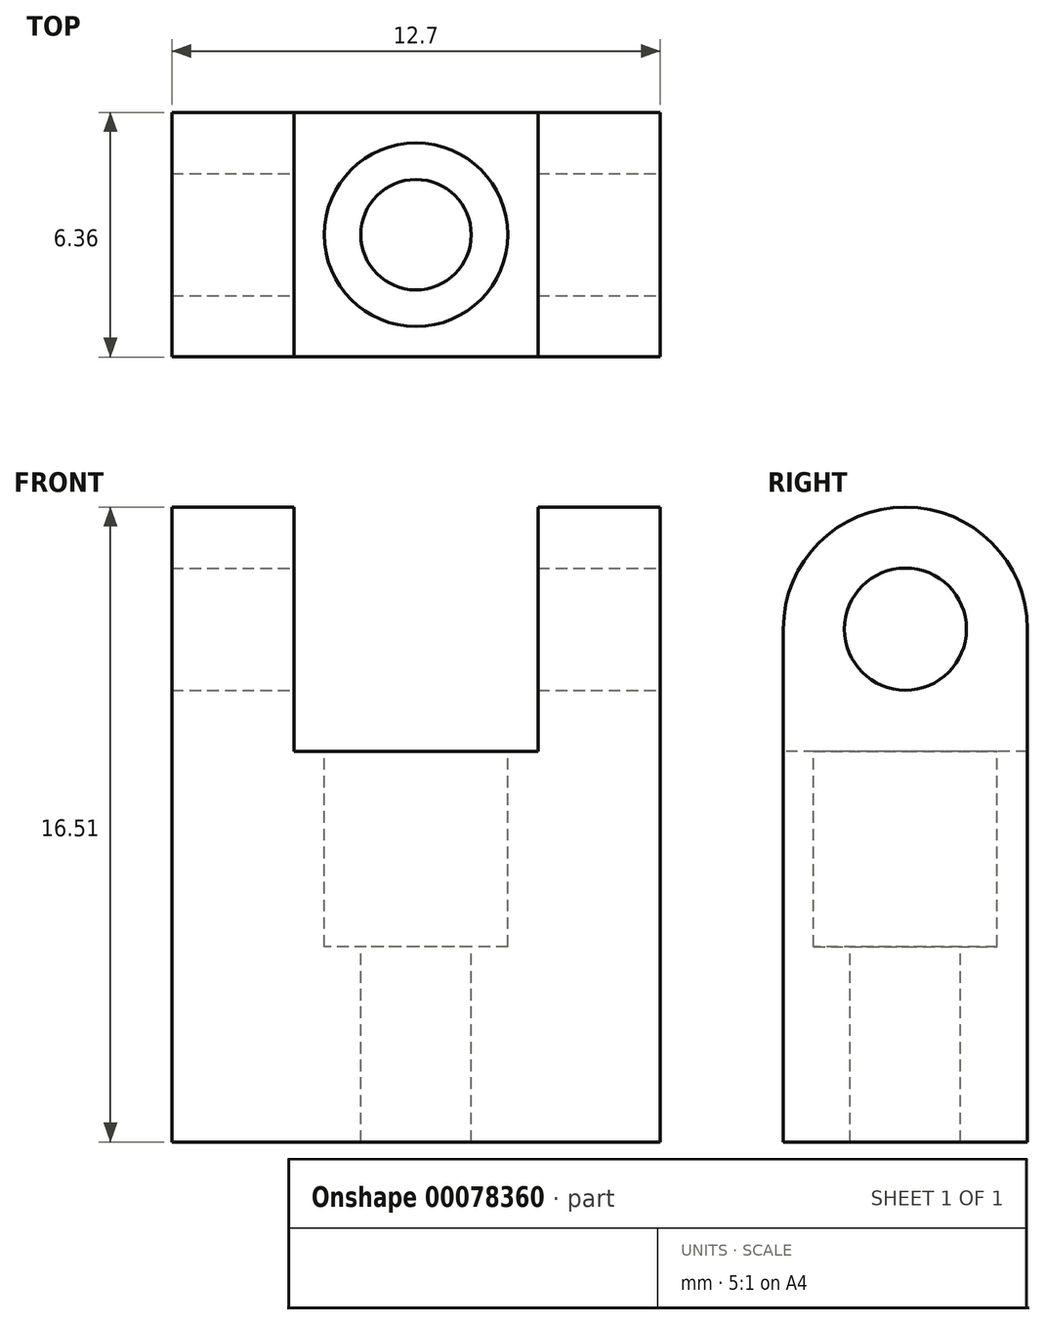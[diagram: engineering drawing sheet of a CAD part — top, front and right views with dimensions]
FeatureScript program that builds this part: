
annotation { "Feature Type Name" : "Feature", "Feature Type Description" : "" }
export const myFeature = defineFeature(function(context is Context, id is Id, definition is map)
    precondition{}
    {
        {
            var Q0;
            Q0=qCreatedBy(makeId("Right.planeOp"),FACE);
            var sketch = newSketch(context, id + "F0", { "sketchPlane" : qUnion([Q0])});
            skLineSegment(sketch, "E0", {"start": v(0, 0) * mm, "end": v(-3.18, 0) * mm});
            skLineSegment(sketch, "E1", {"start": v(-3.18, 0) * mm, "end": v(-3.18, 13.34) * mm});
            skArc(sketch, "E2", {"start": v(3.18, 13.34) * mm, "mid": v(0, 16.51) * mm, "end": v(-3.18, 13.33) * mm});
            skLineSegment(sketch, "E3.MirrorCS", {"start": v(3.18, 0) * mm, "end": v(3.18, 13.34) * mm});
            skLineSegment(sketch, "E4.MirrorCS", {"start": v(0, 0) * mm, "end": v(3.18, 0) * mm});
            skSolve(sketch);
        }
        {
            var Q0;
            Q0 = qSketchRegion(id + "F0", true);
            extrude(context, id + "F1", {"entities" : qUnion([Q0]), "depth" : 12.7 * mm});
        }
        {
            var Q0;
            Q0=makeQuery(id+"F1.opExtrude","CAP_FACE",FACE,{"disambiguationData":[OSD([sQuery(id+"F0.wireOp",EDGE,"E0"),sQuery(id+"F0.wireOp",EDGE,"E1"),sQuery(id+"F0.wireOp",EDGE,"E2"),sQuery(id+"F0.wireOp",EDGE,"E3.MirrorCS"),sQuery(id+"F0.wireOp",EDGE,"E4.MirrorCS")])],"isStart":false});
            var sketch = newSketch(context, id + "F2", { "sketchPlane" : qUnion([Q0])});
            skCircle(sketch, "E5", {"center": v(0, 13.33) * mm, "radius": 1.59 * mm});
            skSolve(sketch);
        }
        {
            var Q0;
            Q0=makeQuery(id+"F2.imprint","IMPRINT",FACE,{"disambiguationData":[TD([[makeQuery(id+"F2.imprint","IMPRINT",EDGE,{"derivedFrom":sQuery(id+"F2.wireOp",EDGE,"E5")}),1.0]])]});
            extrude(context, id + "F3", {"entities" : qUnion([Q0]), "operationType" : NewBodyOperationType.REMOVE, "oppositeDirection" : true, "depth" : 25.4 * mm});
        }
        {
            var Q0;
            Q0=makeQuery(id+"F1.opExtrude","SWEPT_FACE",FACE,{"disambiguationData":[OSD([sQuery(id+"F0.wireOp",EDGE,"E1")])]});
            var sketch = newSketch(context, id + "F4", { "sketchPlane" : qUnion([Q0])});
            skLineSegment(sketch, "E6", {"start": v(6.35, 0) * mm, "end": v(6.35, 10.16) * mm, "construction": true});
            skPoint(sketch, "E6.endSnap0", {"position": v(6.35, 13.33) * mm});
            skLineSegment(sketch, "E7", {"start": v(6.35, 10.16) * mm, "end": v(3.18, 10.16) * mm});
            skLineSegment(sketch, "E8", {"start": v(3.18, 10.16) * mm, "end": v(3.18, 19.15) * mm});
            skLineSegment(sketch, "E9.MirrorCS", {"start": v(9.53, 10.16) * mm, "end": v(9.53, 19.15) * mm});
            skLineSegment(sketch, "E10.MirrorCS", {"start": v(6.35, 10.16) * mm, "end": v(9.53, 10.16) * mm});
            skLineSegment(sketch, "E11", {"start": v(3.18, 19.15) * mm, "end": v(9.53, 19.15) * mm});
            skSolve(sketch);
        }
        {
            var Q0;
            Q0 = qSketchRegion(id + "F4", true);
            extrude(context, id + "F5", {"entities" : qUnion([Q0]), "operationType" : NewBodyOperationType.REMOVE, "oppositeDirection" : true, "depth" : 25.4 * mm});
        }
        {
            var Q0;
            Q0=makeQuery(id+"F5.boolean.opBoolean","COPY",FACE,{"derivedFrom":makeQuery(id+"F5.opExtrude","SWEPT_FACE",FACE,{"disambiguationData":[OSD([sQuery(id+"F4.wireOp",EDGE,"E7"),sQuery(id+"F4.wireOp",EDGE,"E10.MirrorCS")])]})});
            var sketch = newSketch(context, id + "F6", { "sketchPlane" : qUnion([Q0])});
            skLineSegment(sketch, "E12", {"start": v(3.18, 0) * mm, "end": v(9.53, 0) * mm});
            skCircle(sketch, "E13", {"center": v(6.35, 0) * mm, "radius": 1.44 * mm});
            skSolve(sketch);
        }
        {
            var Q0;
            Q0 = qSketchRegion(id + "F6", true);
            extrude(context, id + "F7", {"entities" : qUnion([Q0]), "operationType" : NewBodyOperationType.REMOVE, "oppositeDirection" : true, "depth" : 25.4 * mm});
        }
        {
            var Q0;
            Q0=makeQuery(id+"F5.boolean.opBoolean","COPY",FACE,{"derivedFrom":makeQuery(id+"F5.opExtrude","SWEPT_FACE",FACE,{"disambiguationData":[OSD([sQuery(id+"F4.wireOp",EDGE,"E7"),sQuery(id+"F4.wireOp",EDGE,"E10.MirrorCS")])]})});
            var sketch = newSketch(context, id + "F8", { "sketchPlane" : qUnion([Q0])});
            skCircle(sketch, "E14", {"center": v(6.35, 0) * mm, "radius": 2.39 * mm});
            skSolve(sketch);
        }
        {
            var Q0;
            Q0 = qSketchRegion(id + "F8", true);
            extrude(context, id + "F9", {"entities" : qUnion([Q0]), "operationType" : NewBodyOperationType.REMOVE, "oppositeDirection" : true, "depth" : 5.08 * mm});
        }
    });
